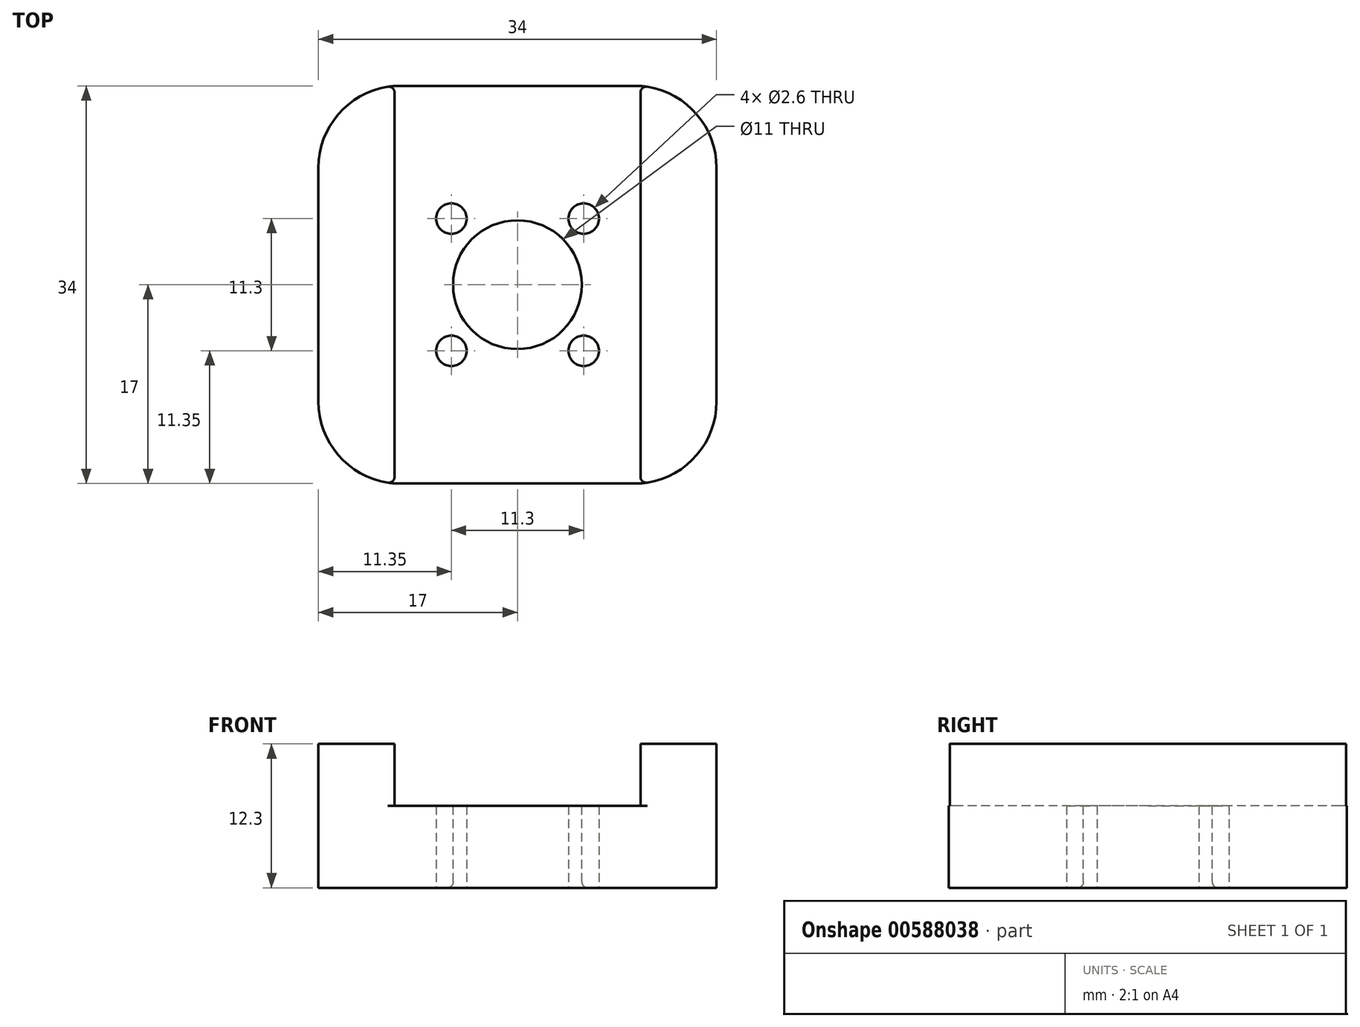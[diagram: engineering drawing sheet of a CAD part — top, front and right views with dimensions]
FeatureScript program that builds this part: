
annotation { "Feature Type Name" : "Feature", "Feature Type Description" : "" }
export const myFeature = defineFeature(function(context is Context, id is Id, definition is map)
    precondition{}
    {
        {
            var Q0;
            Q0=qCreatedBy(makeId("Top.planeOp"),FACE);
            var sketch = newSketch(context, id + "F0", { "sketchPlane" : qUnion([Q0])});
            skLineSegment(sketch, "E0.bottom", {"start": v(-17, 17) * mm, "end": v(17, 17) * mm});
            skLineSegment(sketch, "E0.top", {"start": v(-17, -17) * mm, "end": v(17, -17) * mm});
            skLineSegment(sketch, "E0.left", {"start": v(-17, 17) * mm, "end": v(-17, -17) * mm});
            skLineSegment(sketch, "E0.right", {"start": v(17, 17) * mm, "end": v(17, -17) * mm});
            skPoint(sketch, "E1", {"position": v(0, 17) * mm});
            skPoint(sketch, "E2", {"position": v(17, 0) * mm});
            skSolve(sketch);
        }
        {
            var Q0;
            Q0 = qSketchRegion(id + "F0", true);
            extrude(context, id + "F1", {"entities" : qUnion([Q0]), "depth" : 12.3 * mm, "offsetDistance" : 25 * mm});
        }
        {
            var Q0;
            Q0=makeQuery(id+"F1.opExtrude","CAP_FACE",FACE,{"disambiguationData":[OSD([sQuery(id+"F0.wireOp",EDGE,"E0.bottom"),sQuery(id+"F0.wireOp",EDGE,"E0.top"),sQuery(id+"F0.wireOp",EDGE,"E0.left"),sQuery(id+"F0.wireOp",EDGE,"E0.right")])],"isStart":false});
            var sketch = newSketch(context, id + "F2", { "sketchPlane" : qUnion([Q0])});
            skCircle(sketch, "E3", {"center": v(0, 0) * mm, "radius": 5.5 * mm});
            skSolve(sketch);
        }
        {
            var Q0;
            Q0 = qSketchRegion(id + "F2", true);
            extrude(context, id + "F3", {"entities" : qUnion([Q0]), "operationType" : NewBodyOperationType.REMOVE, "endBound" : BoundingType.THROUGH_ALL, "oppositeDirection" : true, "depth" : 25 * mm, "offsetDistance" : 25 * mm});
        }
        {
            var Q0;
            Q0=makeQuery(id+"F1.opExtrude","CAP_FACE",FACE,{"disambiguationData":[OSD([sQuery(id+"F0.wireOp",EDGE,"E0.bottom"),sQuery(id+"F0.wireOp",EDGE,"E0.top"),sQuery(id+"F0.wireOp",EDGE,"E0.left"),sQuery(id+"F0.wireOp",EDGE,"E0.right")])],"isStart":true});
            var sketch = newSketch(context, id + "F4", { "sketchPlane" : qUnion([Q0])});
            skCircle(sketch, "E4", {"center": v(-5.65, 5.65) * mm, "radius": 1.3 * mm});
            skCircle(sketch, "E5.0.1.0", {"center": v(-5.65, -5.65) * mm, "radius": 1.3 * mm});
            skCircle(sketch, "E5.1.0.0", {"center": v(5.65, 5.65) * mm, "radius": 1.3 * mm});
            skCircle(sketch, "E5.1.1.0", {"center": v(5.65, -5.65) * mm, "radius": 1.3 * mm});
            skLineSegment(sketch, "E5.direction1", {"start": v(-5.65, 5.65) * mm, "end": v(5.65, 5.65) * mm, "construction": true});
            skLineSegment(sketch, "E5.direction2", {"start": v(-5.65, 5.65) * mm, "end": v(-5.65, -5.65) * mm, "construction": true});
            skSolve(sketch);
        }
        {
            var Q0;
            Q0 = qSketchRegion(id + "F4", true);
            extrude(context, id + "F5", {"entities" : qUnion([Q0]), "operationType" : NewBodyOperationType.REMOVE, "endBound" : BoundingType.THROUGH_ALL, "oppositeDirection" : true, "depth" : 25 * mm, "offsetDistance" : 25 * mm});
        }
        {
            var Q0;
            Q0=makeQuery(id+"F1.opExtrude","SWEPT_FACE",FACE,{"disambiguationData":[OSD([sQuery(id+"F0.wireOp",EDGE,"E0.top")])]});
            var sketch = newSketch(context, id + "F6", { "sketchPlane" : qUnion([Q0])});
            skLineSegment(sketch, "E6.bottom", {"start": v(-10.5, 12.3) * mm, "end": v(10.5, 12.3) * mm});
            skLineSegment(sketch, "E6.top", {"start": v(-10.5, 7) * mm, "end": v(10.5, 7) * mm});
            skLineSegment(sketch, "E6.left", {"start": v(-10.5, 12.3) * mm, "end": v(-10.5, 7) * mm});
            skLineSegment(sketch, "E6.right", {"start": v(10.5, 12.3) * mm, "end": v(10.5, 7) * mm});
            skPoint(sketch, "E7", {"position": v(0, 7) * mm});
            skSolve(sketch);
        }
        {
            var Q0;
            Q0 = qSketchRegion(id + "F6", true);
            extrude(context, id + "F7", {"entities" : qUnion([Q0]), "operationType" : NewBodyOperationType.REMOVE, "endBound" : BoundingType.THROUGH_ALL, "oppositeDirection" : true, "depth" : 25 * mm, "offsetDistance" : 25 * mm});
        }
        {
            var Q0;
            Q0=makeQuery(id+"F1.opExtrude","SWEPT_EDGE",EDGE,{"disambiguationData":[OSD([sQuery(id+"F0.wireOp",EDGE,"E0.top"),sQuery(id+"F0.wireOp",EDGE,"E0.left")])]});
            var Q1;
            Q1=makeQuery(id+"F1.opExtrude","SWEPT_EDGE",EDGE,{"disambiguationData":[OSD([sQuery(id+"F0.wireOp",EDGE,"E0.top"),sQuery(id+"F0.wireOp",EDGE,"E0.right")])]});
            var Q2;
            Q2=makeQuery(id+"F1.opExtrude","SWEPT_EDGE",EDGE,{"disambiguationData":[OSD([sQuery(id+"F0.wireOp",EDGE,"E0.bottom"),sQuery(id+"F0.wireOp",EDGE,"E0.right")])]});
            var Q3;
            Q3=makeQuery(id+"F1.opExtrude","SWEPT_EDGE",EDGE,{"disambiguationData":[OSD([sQuery(id+"F0.wireOp",EDGE,"E0.bottom"),sQuery(id+"F0.wireOp",EDGE,"E0.left")])]});
            fillet(context, id + "F8", {"entities" : qUnion([Q0, Q1, Q2, Q3]), "radius" : 7 * mm, "tangentPropagation" : true, "allowEdgeOverflow" : false});
        }
        {
            var Q0;
            Q0=makeQuery(id+"F3.boolean.opBoolean","INTERSECT",EDGE,{"derivedFrom":[makeQuery(id+"F1.opExtrude","CAP_FACE",FACE,{"disambiguationData":[OSD([sQuery(id+"F0.wireOp",EDGE,"E0.bottom"),sQuery(id+"F0.wireOp",EDGE,"E0.top"),sQuery(id+"F0.wireOp",EDGE,"E0.left"),sQuery(id+"F0.wireOp",EDGE,"E0.right")])],"isStart":true}),makeQuery(id+"F3.opExtrude","SWEPT_FACE",FACE,{"disambiguationData":[OSD([sQuery(id+"F2.wireOp",EDGE,"E3")])]})]});
            var Q1;
            Q1=makeQuery(id+"F8.opFillet","BLEND_EDGE",EDGE,{"blendedFrom":[makeQuery(id+"F1.opExtrude","SWEPT_EDGE",EDGE,{"disambiguationData":[OSD([sQuery(id+"F0.wireOp",EDGE,"E0.bottom"),sQuery(id+"F0.wireOp",EDGE,"E0.left")])]}),makeQuery(id+"F7.boolean.opBoolean","COPY",FACE,{"derivedFrom":makeQuery(id+"F7.opExtrude","SWEPT_FACE",FACE,{"disambiguationData":[OSD([sQuery(id+"F6.wireOp",EDGE,"E6.left")])]})})],"blendedInto":[makeQuery(id+"F7.boolean.opBoolean","COPY",FACE,{"derivedFrom":makeQuery(id+"F7.opExtrude","SWEPT_FACE",FACE,{"disambiguationData":[OSD([sQuery(id+"F6.wireOp",EDGE,"E6.left")])]})})]});
            var Q2;
            Q2=makeQuery(id+"F8.opFillet","BLEND_EDGE",EDGE,{"blendedFrom":[makeQuery(id+"F1.opExtrude","SWEPT_EDGE",EDGE,{"disambiguationData":[OSD([sQuery(id+"F0.wireOp",EDGE,"E0.top"),sQuery(id+"F0.wireOp",EDGE,"E0.left")])]}),makeQuery(id+"F7.boolean.opBoolean","COPY",FACE,{"derivedFrom":makeQuery(id+"F7.opExtrude","SWEPT_FACE",FACE,{"disambiguationData":[OSD([sQuery(id+"F6.wireOp",EDGE,"E6.left")])]})})],"blendedInto":[makeQuery(id+"F7.boolean.opBoolean","COPY",FACE,{"derivedFrom":makeQuery(id+"F7.opExtrude","SWEPT_FACE",FACE,{"disambiguationData":[OSD([sQuery(id+"F6.wireOp",EDGE,"E6.left")])]})})]});
            var Q3;
            Q3=makeQuery(id+"F8.opFillet","BLEND_EDGE",EDGE,{"blendedFrom":[makeQuery(id+"F1.opExtrude","SWEPT_EDGE",EDGE,{"disambiguationData":[OSD([sQuery(id+"F0.wireOp",EDGE,"E0.top"),sQuery(id+"F0.wireOp",EDGE,"E0.right")])]}),makeQuery(id+"F7.boolean.opBoolean","COPY",FACE,{"derivedFrom":makeQuery(id+"F7.opExtrude","SWEPT_FACE",FACE,{"disambiguationData":[OSD([sQuery(id+"F6.wireOp",EDGE,"E6.right")])]})})],"blendedInto":[makeQuery(id+"F7.boolean.opBoolean","COPY",FACE,{"derivedFrom":makeQuery(id+"F7.opExtrude","SWEPT_FACE",FACE,{"disambiguationData":[OSD([sQuery(id+"F6.wireOp",EDGE,"E6.right")])]})})]});
            var Q4;
            Q4=makeQuery(id+"F8.opFillet","BLEND_EDGE",EDGE,{"blendedFrom":[makeQuery(id+"F1.opExtrude","SWEPT_EDGE",EDGE,{"disambiguationData":[OSD([sQuery(id+"F0.wireOp",EDGE,"E0.bottom"),sQuery(id+"F0.wireOp",EDGE,"E0.right")])]}),makeQuery(id+"F7.boolean.opBoolean","COPY",FACE,{"derivedFrom":makeQuery(id+"F7.opExtrude","SWEPT_FACE",FACE,{"disambiguationData":[OSD([sQuery(id+"F6.wireOp",EDGE,"E6.right")])]})})],"blendedInto":[makeQuery(id+"F7.boolean.opBoolean","COPY",FACE,{"derivedFrom":makeQuery(id+"F7.opExtrude","SWEPT_FACE",FACE,{"disambiguationData":[OSD([sQuery(id+"F6.wireOp",EDGE,"E6.right")])]})})]});
            fillet(context, id + "F9", {"entities" : qUnion([Q0, Q1, Q2, Q3, Q4]), "radius" : 0.5 * mm, "tangentPropagation" : true, "allowEdgeOverflow" : false});
        }
    });
